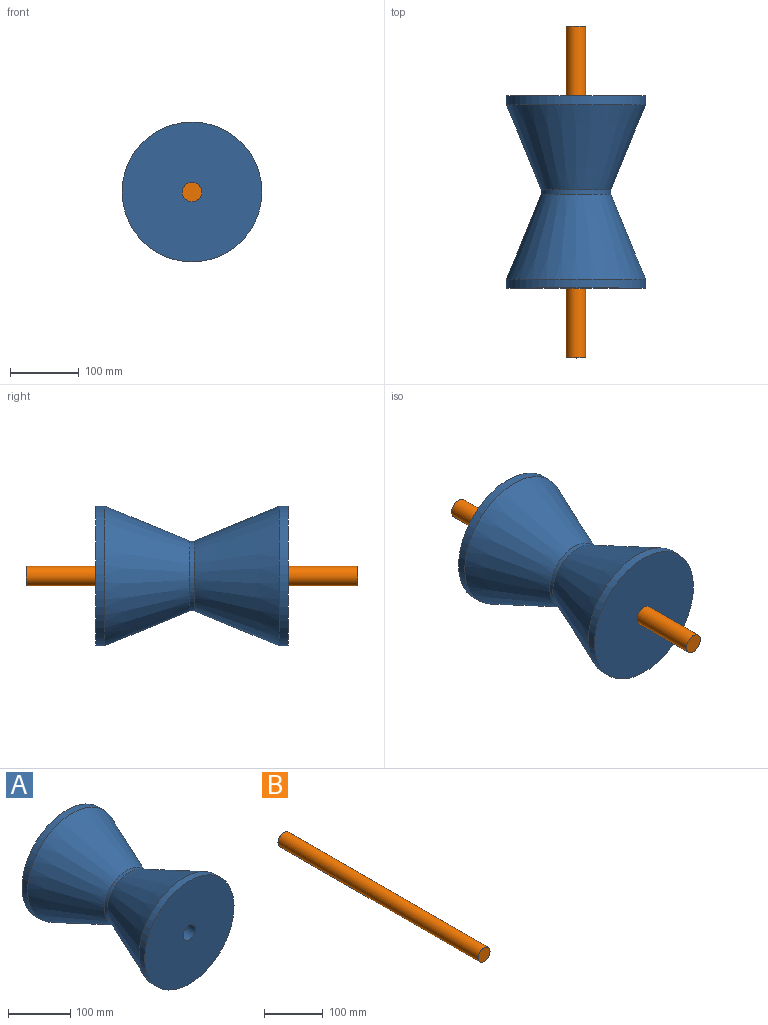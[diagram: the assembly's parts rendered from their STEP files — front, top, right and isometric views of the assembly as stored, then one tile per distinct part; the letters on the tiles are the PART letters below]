
ASSEMBLY  parts=2 mates=1
PART A: 8 faces, bbox 203.2x279.4x203.2 mm
  f0: cylinder r=101.6mm len=203.2mm, axis (0,-1,0), area 8107.3mm2, adj f1,f6
  f1: plane 203.2x203.2mm, normal (0,-1,0), area 31788mm2, adj f0,f7
  f2: plane 203.2x203.2mm, normal (0,1,0), area 31788mm2, adj f3,f7
  f3: cylinder r=101.6mm len=203.2mm, axis (0,-1,0), area 8107.3mm2, adj f2,f4
  f4: cone r=50.8mm half-angle=22.3deg, axis (0,1,0), area 64080mm2, adj f3,f5
  f5: cylinder r=50.8mm len=101.6mm, axis (0,-1,0), area 2026.8mm2, adj f4,f6
  f6: cone r=50.8mm half-angle=22.3deg, axis (0,-1,0), area 64080mm2, adj f0,f5
  f7: cylinder r=14.29mm len=279.4mm, axis (0,-1,0), area 25082mm2, adj f1,f2
PART B: 3 faces, bbox 28.6x482.6x28.6 mm
  f0: cylinder r=14.29mm len=482.6mm, axis (0,-1,0), area 43323.5mm2, adj f1,f2
  f1: plane 28.58x28.58mm, normal (0,1,0), area 641.3mm2, adj f0
  f2: plane 28.58x28.58mm, normal (0,-1,0), area 641.3mm2, adj f0
PLACE A t=(0,-139.7,0)mm
PLACE B t=(0,-139.7,0)mm
MATE fastened B.f0 <-> A.f0  axis (0,-1,0) through (0,0,0)mm
